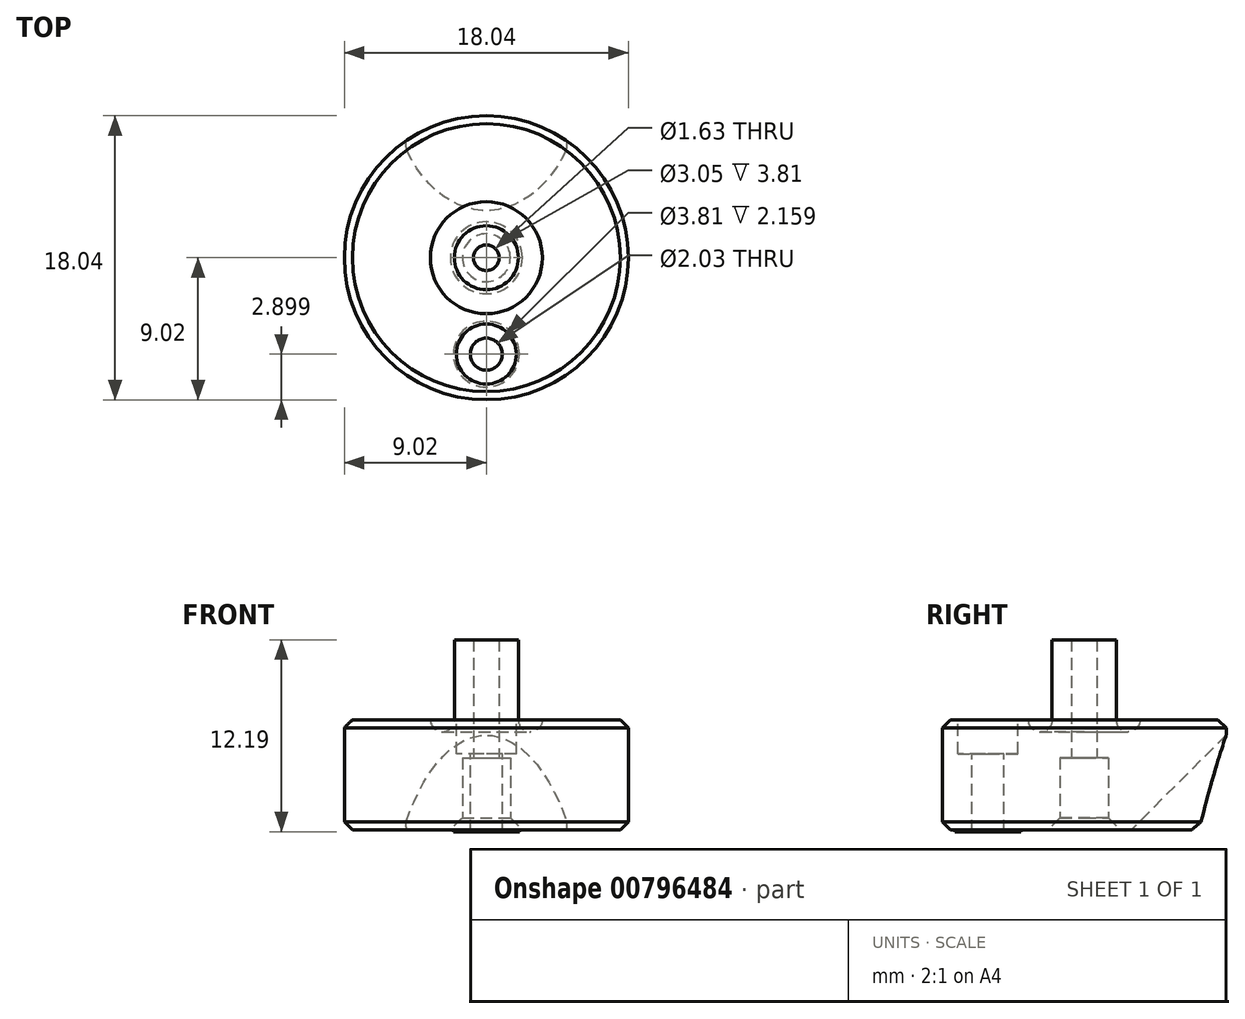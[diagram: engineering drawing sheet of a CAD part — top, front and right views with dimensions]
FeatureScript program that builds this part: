
annotation { "Feature Type Name" : "Feature", "Feature Type Description" : "" }
export const myFeature = defineFeature(function(context is Context, id is Id, definition is map)
    precondition{}
    {
        {
            var Q0;
            Q0=qCreatedBy(makeId("Front.planeOp"),FACE);
            var sketch = newSketch(context, id + "F0", { "sketchPlane" : qUnion([Q0])});
            skLineSegment(sketch, "E0", {"start": v(0.81, 12.2) * mm, "end": v(2.03, 12.2) * mm});
            skLineSegment(sketch, "E1", {"start": v(2.03, 12.2) * mm, "end": v(2.03, 7.11) * mm});
            skLineSegment(sketch, "E2", {"start": v(9.02, 7.11) * mm, "end": v(9.02, 0.13) * mm});
            skLineSegment(sketch, "E3", {"start": v(0.81, 12.2) * mm, "end": v(0.81, 4.7) * mm});
            skLineSegment(sketch, "E4", {"start": v(0.81, 4.7) * mm, "end": v(1.52, 4.7) * mm});
            skLineSegment(sketch, "E5", {"start": v(1.52, 4.7) * mm, "end": v(1.52, 0.13) * mm});
            skLineSegment(sketch, "E6", {"start": v(1.52, 0.13) * mm, "end": v(9.02, 0.13) * mm});
            skLineSegment(sketch, "E7", {"start": v(0, 0) * mm, "end": v(0, 16.84) * mm});
            skArc(sketch, "E8", {"start": v(2.03, 7.11) * mm, "mid": v(2.8, 6.35) * mm, "end": v(3.56, 7.11) * mm});
            skLineSegment(sketch, "E9.trimOffspring", {"start": v(3.56, 7.11) * mm, "end": v(9.02, 7.11) * mm});
            skSolve(sketch);
        }
        {
            var Q0;
            Q0 = qSketchRegion(id + "F0", true);
            var Q1;
            Q1=sQuery(id+"F0.wireOp",EDGE,"E7");
            revolve(context, id + "F1", {"surfaceOperationType" : NewSurfaceOperationType.NEW, "entities" : qUnion([Q0]), "axis" : qUnion([Q1]), "revolveType" : RevolveType.FULL});
        }
        {
            var Q0;
            Q0=makeQuery(id+"F1.opRevolve","SWEPT_FACE",FACE,{"disambiguationData":[OSD([sQuery(id+"F0.wireOp",EDGE,"E6")])]});
            var sketch = newSketch(context, id + "F2", { "sketchPlane" : qUnion([Q0])});
            skCircle(sketch, "E10", {"center": v(0, 6.12) * mm, "radius": 2.1 * mm});
            skSolve(sketch);
        }
        {
            var Q0;
            Q0 = qSketchRegion(id + "F2", true);
            extrude(context, id + "F3", {"entities" : qUnion([Q0]), "operationType" : NewBodyOperationType.ADD, "depth" : 0.13 * mm, "offsetDistance" : 25.4 * mm});
        }
        {
            var Q0;
            Q0=qCreatedBy(makeId("Right.planeOp"),FACE);
            var sketch = newSketch(context, id + "F4", { "sketchPlane" : qUnion([Q0])});
            skLineSegment(sketch, "E11", {"start": v(0, 0) * mm, "end": v(0, -10.91) * mm, "construction": true});
            skSolve(sketch);
        }
        {
            var Q0;
            Q0=makeQuery(id+"F1.opRevolve","SWEPT_FACE",FACE,{"disambiguationData":[OSD([sQuery(id+"F0.wireOp",EDGE,"E9.trimOffspring")])]});
            var sketch = newSketch(context, id + "F5", { "sketchPlane" : qUnion([Q0])});
            skPoint(sketch, "E12.orphan", {"position": v(1.9, -6.12) * mm});
            skCircle(sketch, "E13.converted", {"center": v(0, -6.12) * mm, "radius": 1.9 * mm});
            skSolve(sketch);
        }
        {
            var Q0;
            Q0 = qSketchRegion(id + "F5", true);
            extrude(context, id + "F6", {"entities" : qUnion([Q0]), "operationType" : NewBodyOperationType.REMOVE, "oppositeDirection" : true, "depth" : 2.16 * mm, "offsetDistance" : 25.4 * mm});
        }
        {
            var Q0;
            Q0=makeQuery(id+"F6.boolean.opBoolean","COPY",FACE,{"derivedFrom":makeQuery(id+"F6.opExtrude","CAP_FACE",FACE,{"disambiguationData":[OSD([sQuery(id+"F5.wireOp",EDGE,"E13.converted")])],"isStart":false})});
            var sketch = newSketch(context, id + "F7", { "sketchPlane" : qUnion([Q0])});
            skCircle(sketch, "E14", {"center": v(0, -6.12) * mm, "radius": 1.02 * mm});
            skSolve(sketch);
        }
        {
            var Q0;
            Q0 = qSketchRegion(id + "F7", true);
            var Q1;
            Q1=makeQuery(id+"F3.opExtrude","CAP_FACE",FACE,{"disambiguationData":[OSD([sQuery(id+"F2.wireOp",EDGE,"E10")])],"isStart":false});
            extrude(context, id + "F8", {"entities" : qUnion([Q0]), "operationType" : NewBodyOperationType.REMOVE, "endBound" : BoundingType.UP_TO_SURFACE, "oppositeDirection" : true, "depth" : 25.4 * mm, "endBoundEntityFace" : qUnion([Q1]), "offsetDistance" : 25.4 * mm});
        }
        {
            var Q0;
            Q0=qCreatedBy(makeId("Front.planeOp"),FACE);
            var sketch = newSketch(context, id + "F9", { "sketchPlane" : qUnion([Q0])});
            skLineSegment(sketch, "E15", {"start": v(0, 0) * mm, "end": v(58, 0) * mm, "construction": true});
            skSolve(sketch);
        }
        {
            var Q0;
            Q0=sQuery(id+"F9.wireOp",EDGE,"E15");
            cPlane(context, id + "F10", {"entities" : qUnion([Q0]), "cplaneType" : CPlaneType.LINE_ANGLE, "offset" : 25.4 * mm, "angle" : 45 * degree, "width" : 152.4 * mm, "height" : 152.4 * mm});
        }
        {
            var Q0;
            Q0=qCreatedBy(id+"F10.planeOp",FACE);
            var sketch = newSketch(context, id + "F11", { "sketchPlane" : qUnion([Q0])});
            skCircle(sketch, "E16", {"center": v(0, -8.13) * mm, "radius": 6.1 * mm});
            skPoint(sketch, "E16.first.point", {"position": v(5.28, -5.08) * mm});
            skPoint(sketch, "E16.second.point", {"position": v(0, -2.03) * mm});
            skPoint(sketch, "E16.third.point", {"position": v(-5.4, -5.31) * mm});
            skLineSegment(sketch, "E17", {"start": v(0, 0) * mm, "end": v(0, -16.67) * mm, "construction": true});
            skSolve(sketch);
        }
        {
            var Q0;
            Q0 = qSketchRegion(id + "F11", true);
            extrude(context, id + "F12", {"entities" : qUnion([Q0]), "operationType" : NewBodyOperationType.REMOVE, "endBound" : BoundingType.THROUGH_ALL, "depth" : 25.4 * mm, "offsetDistance" : 25.4 * mm});
        }
        {
            var Q0;
            Q0=makeQuery(id+"F1.opRevolve","SWEPT_EDGE",EDGE,{"disambiguationData":[OSD([sQuery(id+"F0.wireOp",EDGE,"E5"),sQuery(id+"F0.wireOp",EDGE,"E6")])]});
            var Q1;
            Q1=makeQuery(id+"FUBxC1yStt3OMup_1.-2.F6.boolean.opBoolean","COPY",EDGE,{"derivedFrom":makeQuery(id+"FUBxC1yStt3OMup_1.-2.F6.opExtrude","CAP_EDGE",EDGE,{"disambiguationData":[OSD([sQuery(id+"F5.wireOp",EDGE,"JWmOvO4F-mvez-cvsf-xhD7-6kZY9cxx8prf")])],"isStart":true})});
            var Q2;
            Q2=makeQuery(id+"F6.boolean.opBoolean","COPY",EDGE,{"derivedFrom":makeQuery(id+"F6.opExtrude","CAP_EDGE",EDGE,{"disambiguationData":[OSD([sQuery(id+"F5.wireOp",EDGE,"JWmOvO4F-mvez-cvsf-xhD7-6kZY9cxx8prf")])],"isStart":true})});
            var Q3;
            Q3=makeQuery(id+"FUBxC1yStt3OMup_1.-1.F6.boolean.opBoolean","COPY",EDGE,{"derivedFrom":makeQuery(id+"FUBxC1yStt3OMup_1.-1.F6.opExtrude","CAP_EDGE",EDGE,{"disambiguationData":[OSD([sQuery(id+"F5.wireOp",EDGE,"JWmOvO4F-mvez-cvsf-xhD7-6kZY9cxx8prf")])],"isStart":true})});
            chamfer(context, id + "F13", {"entities" : qUnion([Q0, Q1, Q2, Q3]), "width" : 0.76 * mm, "tangentPropagation" : true});
        }
        {
            var Q0;
            {var subQ0=sQuery(id+"F0.wireOp",EDGE,"E2");var subQ1=sQuery(id+"F11.wireOp",EDGE,"E16");var subQ2=sQuery(id+"F0.wireOp",EDGE,"E6");Q0=makeQuery(id+"FXWYidmT5VWI4eV_1.2.F12.boolean.opBoolean","SPLIT",EDGE,{"disambiguationData":[TD([makeQuery(id+"F12.boolean.opBoolean","COPY",FACE,{"derivedFrom":makeQuery(id+"F12.opExtrude","SWEPT_FACE",FACE,{"disambiguationData":[OSD([subQ1])]})})])],"derivedFrom":makeQuery(id+"FXWYidmT5VWI4eV_1.1.F12.boolean.opBoolean","SPLIT",EDGE,{"disambiguationData":[OD(0.0)],"derivedFrom":makeQuery(id+"F1.opRevolve","SWEPT_EDGE",EDGE,{"disambiguationData":[OSD([subQ0,subQ2])]})})});}
            var Q1;
            Q1=makeQuery(id+"FXWYidmT5VWI4eV_1.1.F12.boolean.opBoolean","SPLIT",EDGE,{"disambiguationData":[OD(1.0)],"derivedFrom":makeQuery(id+"F1.opRevolve","SWEPT_EDGE",EDGE,{"disambiguationData":[OSD([sQuery(id+"F0.wireOp",EDGE,"E2"),sQuery(id+"F0.wireOp",EDGE,"E6")])]})});
            var Q2;
            {var subQ0=sQuery(id+"F0.wireOp",EDGE,"E2");var subQ1=sQuery(id+"F0.wireOp",EDGE,"E6");var subQ2=sQuery(id+"F11.wireOp",EDGE,"E16");Q2=makeQuery(id+"FXWYidmT5VWI4eV_1.2.F12.boolean.opBoolean","SPLIT",EDGE,{"disambiguationData":[TD([makeQuery(id+"FXWYidmT5VWI4eV_1.1.F12.boolean.opBoolean","COPY",FACE,{"derivedFrom":makeQuery(id+"FXWYidmT5VWI4eV_1.1.F12.opExtrude","SWEPT_FACE",FACE,{"disambiguationData":[OSD([subQ2])]})})])],"derivedFrom":makeQuery(id+"FXWYidmT5VWI4eV_1.1.F12.boolean.opBoolean","SPLIT",EDGE,{"disambiguationData":[OD(0.0)],"derivedFrom":makeQuery(id+"F1.opRevolve","SWEPT_EDGE",EDGE,{"disambiguationData":[OSD([subQ0,subQ1])]})})});}
            var Q3;
            Q3=makeQuery(id+"F1.opRevolve","SWEPT_EDGE",EDGE,{"disambiguationData":[OSD([sQuery(id+"F0.wireOp",EDGE,"E2"),sQuery(id+"F0.wireOp",EDGE,"E9.trimOffspring")])]});
            chamfer(context, id + "F14", {"entities" : qUnion([Q0, Q1, Q2, Q3]), "width" : 0.5 * mm, "tangentPropagation" : true});
        }
    });
